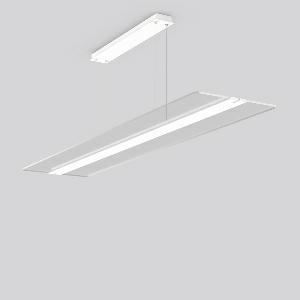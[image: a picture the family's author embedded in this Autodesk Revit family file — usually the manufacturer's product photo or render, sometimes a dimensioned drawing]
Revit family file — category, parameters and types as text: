
# Revit family: twindot_s_312265_002_1_730_f5b3
name_source: partatom
category: Lighting Fixtures
units: mm (PartAtom-declared; Revit-internal decimal feet)

## family parameters
Cut with Voids When Loaded = No
Host = Face
Light Source = No
Part Type = Normal
Room Calculation Point = No
Round Connector Dimension = Use Diameter
Shared = No

## types (1)
- TWINDOT S (1 x LED Modul 840, 8100 lm, 4000)
    Apparent Load = 62 VA
    CIE Flux Codes = 47 77 94 55 100
    Color Rendering = 80
    Color Temperature = 4000
    Default Elevation = 1800 mm
    Description = Series: TWINDOT S
LED pendant luminaire with extremely flat and frameless appearance. Middle bar made of aluminium extrusion profile, powder-coated. Transparent light guide made of UV-resistant acrylic glass (PMMA) with TWINDOT prismatic. Light control with perfectly glare-free TWINDOT technology for pleasantly gentle light with soft shadows. Even and wide indirect and direct light distribution. Direct 55%, indirect 45% light emission. 4-point steel cable suspension, steplessly adjustable. Converter integrated in the canopy (powder-coated white). Power supply through suspension cable. 
Colour: traffic white, matt (RAL 9016)
Length: 1500 mm
Width: 350 mm
Height: 20 mm
Suspension length: 500-1200 mm
Lamp: LED
Socket: without socket
Colour temperature: 4000K
Colour rendering index (CRI): 80
System power: 62 W
Rated luminous flux: 8100 lm
Luminous efficiency: 131 lm/W
Control gear: Dimmable Bluetooth converter
Protection class: I
Type of protection: IP 20
    Height = 20 mm  [stored 0.0656168 ft]
    Lamp = 1 x LED Modul 840
    Lamp Light Flux = 8100 lm
    Lamp count = 1
    Length = 1500 mm
    Lifetime = 50000 h
    Luminous efficacy = 131 lm/W
    Manufacturer = RZB
    ModVariant = No
    Model = 312265.002.1.730
    Mounting Place = Ceiling
    Mounting Type = Pendant
    Number of Poles = 1
    OnlyDefault = Yes
    Power Factor = 1
    Product Name = TWINDOT S
    Product group = Pendant modular luminaires
    ProductGroupID = 906
    Protection Class = Protection class I
    Protection Degree = IP 20
    RLX_Detail_Level = 1
    RLX_Emergency_Light_Flux = 0 lm
    RLX_Emergency_Type = 0
    RLX_Emergency_Type_DB = No
    RlxData = <blob elided: 36569 chars, md5=13eb572a>
    Socket = socket
    Standby Power = 0 W
    System Light Flux = 8100 lm
    System Power = 62 W
    Type Comments = Product without accessories
    Type Image = 312265.002.jpg
    URL = http://relux.com
    VarID = ---
    Voltage = 230 V
    Voltage Range = 220-240 V
    Weight = 0.00 kg
    Width = 350 mm

note: [stored X ft] marks values corroborated as IEEE doubles in the binary element streams (Revit-internal decimal feet)

## geometry (parser evidence)
native form markers: Blend x4, Sweep x15
no freeform markers — native parametric forms only
